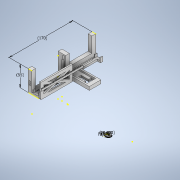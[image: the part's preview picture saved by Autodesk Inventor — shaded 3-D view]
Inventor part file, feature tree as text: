
AUTODESK INVENTOR PART (.ipt)
format: ipt  version: 2020 (Build 240168000, 168)  size: 1,040,384 bytes
history: native  units: mm
features: sketch x63, extrude x47, pattern_circular x1, pattern_linear x1
ambient origin geometry x8: Origin, YZ Plane, XZ Plane, XY Plane, X Axis, Y Axis, Z Axis, Center Point
bodies: Solid1 (feature_tree)
feature tree (112):
  extrude  "Extrusion1"  Depth=200.0mm
  extrude  "Extrusion2"  Depth=100.0mm
  extrude  "Extrusion3"  Depth=20.0mm
  extrude  "Extrusion4"  Depth=10.0mm
  extrude  "Extrusion5"  Depth=100.0mm
  extrude  "Extrusion6"  Depth=10.0mm
  extrude  "Extrusion7"  Depth=10.0mm TaperAngle=0.0deg
  extrude  "Extrusion8"  Depth=50.0mm TaperAngle=0.0deg
  extrude  "Extrusion9"  Depth=10.0mm TaperAngle=0.0deg
  extrude  "Extrusion10"  Depth=3.0mm
  extrude  "Extrusion11"  Depth=1.5mm
  sketch  "Sketch14"  dims[d28=1.0mm d29=1.0mm]
  extrude  "Extrusion12"  Depth=1.0mm
  extrude  "Extrusion13"  Depth=1.5mm
  extrude  "Extrusion14"  Depth=5.0mm TaperAngle=0.0deg
  extrude  "Extrusion15"  Depth=5.0mm TaperAngle=0.0deg
  sketch  "Sketch19"  dims[d45=5.0mm d46=0.0mm d47=70.0mm]
  extrude  "Extrusion16"  Depth=5.0mm TaperAngle=0.0deg
  sketch  "Sketch21"  dims[d51=80.75mm d52=0.0mm d53=10.0mm d54=0.0mm]
  extrude  "Extrusion17"  Depth=70.0mm
  extrude  "Extrusion18"  Depth=5.0mm TaperAngle=0.0deg
  extrude  "Extrusion19"  Depth=10.0mm TaperAngle=0.0deg
  extrude  "Extrusion20"  Depth=194.25mm TaperAngle=0.0deg
  extrude  "Extrusion21"  Depth=40.0mm
  extrude  "Extrusion24"  Depth=88.0mm TaperAngle=0.0deg
  extrude  "Extrusion25"  Depth=8.0mm
  extrude  "Extrusion26"  Depth=3.0mm
  extrude  "Extrusion27"  Depth=72.0mm TaperAngle=0.0deg
  extrude  "Extrusion28"  Depth=1.5mm
  extrude  "Extrusion29"  Depth=1.5mm TaperAngle=0.0deg
  extrude  "Extrusion30"  Depth=6.0mm
  extrude  "Extrusion31"  Depth=1.0mm
  extrude  "Extrusion32"  Depth=1.0mm
  extrude  "Extrusion33"  Depth=6.0mm
  pattern_circular  "Circular Pattern1"  Count=21 Angle=360.0deg
  extrude  "Extrusion34"  Depth=26.0mm TaperAngle=0.0deg
  extrude  "Extrusion35"  Depth=8.0mm
  sketch  "Sketch44"  dims[d102=1.0mm]
  extrude  "Extrusion36"  Depth=8.0mm
  extrude  "Extrusion37"  Depth=45.0mm TaperAngle=0.0deg
  extrude  "Extrusion40"  Depth=16.0mm
  extrude  "Extrusion41"  Depth=8.0mm
  extrude  "Extrusion42"  Depth=8.0mm
  extrude  "Extrusion43"  Depth=2.0mm TaperAngle=0.0deg
  extrude  "Extrusion44"  Depth=10.9mm
  extrude  "Extrusion45"  Depth=23.0mm
  extrude  "Extrusion46"  Depth=10.0mm
  sketch  "Sketch58"  dims[d116=1.0mm]
  sketch  "Sketch59"  dims[d117=2.0mm]
  sketch  "Sketch60"  dims[d118=4.3mm]
  extrude  "Extrusion47"  Depth=2.0mm TaperAngle=0.0deg
  extrude  "Extrusion48"  Depth=4.0mm TaperAngle=0.0deg
  pattern_linear  "Rectangular Pattern1"  Spacing1=4.0mm  [1 undecoded]
  extrude  "Extrusion49"  Depth=4.0mm
  sketch  "Sketch64"  dims[d123=10.1mm]
  extrude  "Extrusion50"  Depth=4.0mm TaperAngle=0.0deg
  sketch  "Sketch66"  dims[d133=24.5mm d134=0.0mm]
  sketch  "Sketch67"  dims[d135=1.0mm]
  extrude  "Extrusion51"  Depth=4.0mm TaperAngle=0.0deg
  sketch  "Sketch69"  dims[d137=22.68928mm]
  sketch  "Sketch70"  dims[d138=26.0mm d139=0.0mm d140=210.0mm d141=360.0deg]
  sketch  "Sketch71"  dims[d143=24.5mm d144=0.0mm d145=26.0mm d146=0.0mm]
  sketch  "Sketch72"  dims[d147=8.0mm d148=8.0mm]
  sketch  "Sketch73"  dims[d149=8.0mm d150=8.0mm]
  sketch  "Sketch74"  dims[d151=4.5mm d152=0.0mm d153=45.0mm d154=0.0mm d159=16.0mm d160=8.0mm d161=8.0mm d162=30.5mm d163=0.0mm d164=10.9mm d165=23.0mm d166=10.0mm d167=30.5mm d168=0.0mm d169=4.0mm d170=0.0mm d171=4.0mm d172=4.0mm d173=4.0mm d174=0.0mm d175=4.0mm d176=0.0mm d177=10.0mm d178=0.0mm d179=6.0mm d180=8.0mm d181=8.0mm d182=2.0mm d183=0.0mm d184=0.5mm d185=16.954627mm d187=0.5mm d188=12.002203mm d189=13.453434mm d190=4.0mm d191=2.0mm d192=0.0mm d193=1.45mm d194=2.075641mm d195=2.0mm d206=0.5mm d209=0.5mm d210=2.0mm d211=0.0mm d212=550.0mm d214=2.0mm d215=4.0mm d216=0.0mm d217=4.0mm d218=0.0mm d219=170.0mm d220=55.0mm d221=150.0deg d222=12.5mm d223=0.0mm d224=2.0mm]
  sketch  "Sketch1"  dims[d0=200.0mm d1=200.0mm]
  sketch  "Sketch2"  dims[d2=100.0mm d3=100.0mm]
  sketch  "Sketch3"  dims[d4=50.0mm d5=0.0mm d6=20.0mm]
  sketch  "Sketch4"  dims[d7=50.0mm d8=0.0mm d9=10.0mm]
  sketch  "Sketch5"  dims[d10=40.0mm d11=100.0mm]
  sketch  "Sketch6"  dims[d12=10.0mm d13=10.0mm]
  sketch  "Sketch8"  dims[d14=10.0mm d15=34.75mm d16=0.0mm]
  sketch  "Sketch9"  dims[d17=10.0mm d18=50.0mm d19=0.0mm]
  sketch  "Sketch11"  dims[d20=3.0mm d21=10.0mm d22=0.0mm]
  sketch  "Sketch12"  dims[d23=47.0mm d24=0.0mm d25=3.0mm]
  sketch  "Sketch13"  dims[d26=1.5mm d27=1.5mm]
  sketch  "Sketch15"  dims[d30=5.0mm d31=0.0mm d32=1.5mm]
  sketch  "Sketch16"  dims[d33=1.5mm d34=5.0mm d35=0.0mm]
  sketch  "Sketch17"  dims[d38=5.0mm d39=379.25mm d40=0.0mm]
  sketch  "Sketch18"  dims[d41=5.0mm d42=261.5mm d43=0.0mm]
  sketch  "Sketch20"  dims[d48=10.0mm d49=5.0mm d50=0.0mm]
  sketch  "Sketch22"  dims[d55=10.0mm d56=0.0mm d57=194.25mm d58=0.0mm]
  sketch  "Sketch23"  dims[d59=3.5mm d60=40.0mm]
  sketch  "Sketch24"  dims[d61=88.0mm d62=0.0mm d63=88.0mm d64=0.0mm]
  sketch  "Sketch25"  dims[d65=175.25mm d66=0.0mm d67=8.0mm]
  sketch  "Sketch28"  dims[d68=3.5mm d69=3.0mm]
  sketch  "Sketch31"  dims[d70=175.25mm d71=0.0mm d72=72.0mm d73=0.0mm]
  sketch  "Sketch32"  dims[d78=14.25mm d79=0.0mm d80=1.5mm]
  sketch  "Sketch33"  dims[d81=1.5mm d82=246.0mm d83=0.0mm]
  sketch  "Sketch34"  dims[d84=12.5mm d85=6.0mm]
  sketch  "Sketch35"  dims[d86=1.0mm d88=2.1mm]
  sketch  "Sketch36"  dims[d90=4.0mm d91=1.0mm]
  sketch  "Sketch38"  dims[d92=7.0mm d93=0.0mm d94=6.0mm]
  sketch  "Sketch39"  dims[d95=7.0mm d96=0.0mm]
  sketch  "Sketch40"  dims[d97=12.5mm]
  sketch  "Sketch41"  dims[d98=6.0mm]
  sketch  "Sketch42"  dims[d100=2.1mm]
  sketch  "Sketch43"  dims[d101=2.1mm]
  sketch  "Sketch45"  dims[d103=2.0mm]
  sketch  "Sketch46"  dims[d104=1.0mm]
  sketch  "Sketch49"  dims[d105=2.0mm]
  sketch  "Sketch50"  dims[d106=7.0mm d107=0.0mm]
  sketch  "Sketch51"  dims[d108=6.0mm]
  sketch  "Sketch52"  dims[d109=7.0mm d110=0.0mm]
  sketch  "Sketch53"  dims[d113=2.1mm]
  sketch  "Sketch56"  dims[d114=1.0mm]
  sketch  "Sketch57"  dims[d115=2.0mm]
  sketch  "Sketch61"  dims[d119=84.0mm]
  sketch  "Sketch62"  dims[d120=9.25mm d121=0.0mm]
  sketch  "Sketch63"  dims[d122=5.1mm]
  sketch  "Sketch65"  dims[d124=24.5mm d125=0.0mm]
  sketch  "Sketch68"  dims[d136=8.726646mm]
note: 1 required parameter value undecoded (feature->parameter linkage not recoverable at this tier; creation-order binding heuristic only, values carry confidence <= 0.55)
